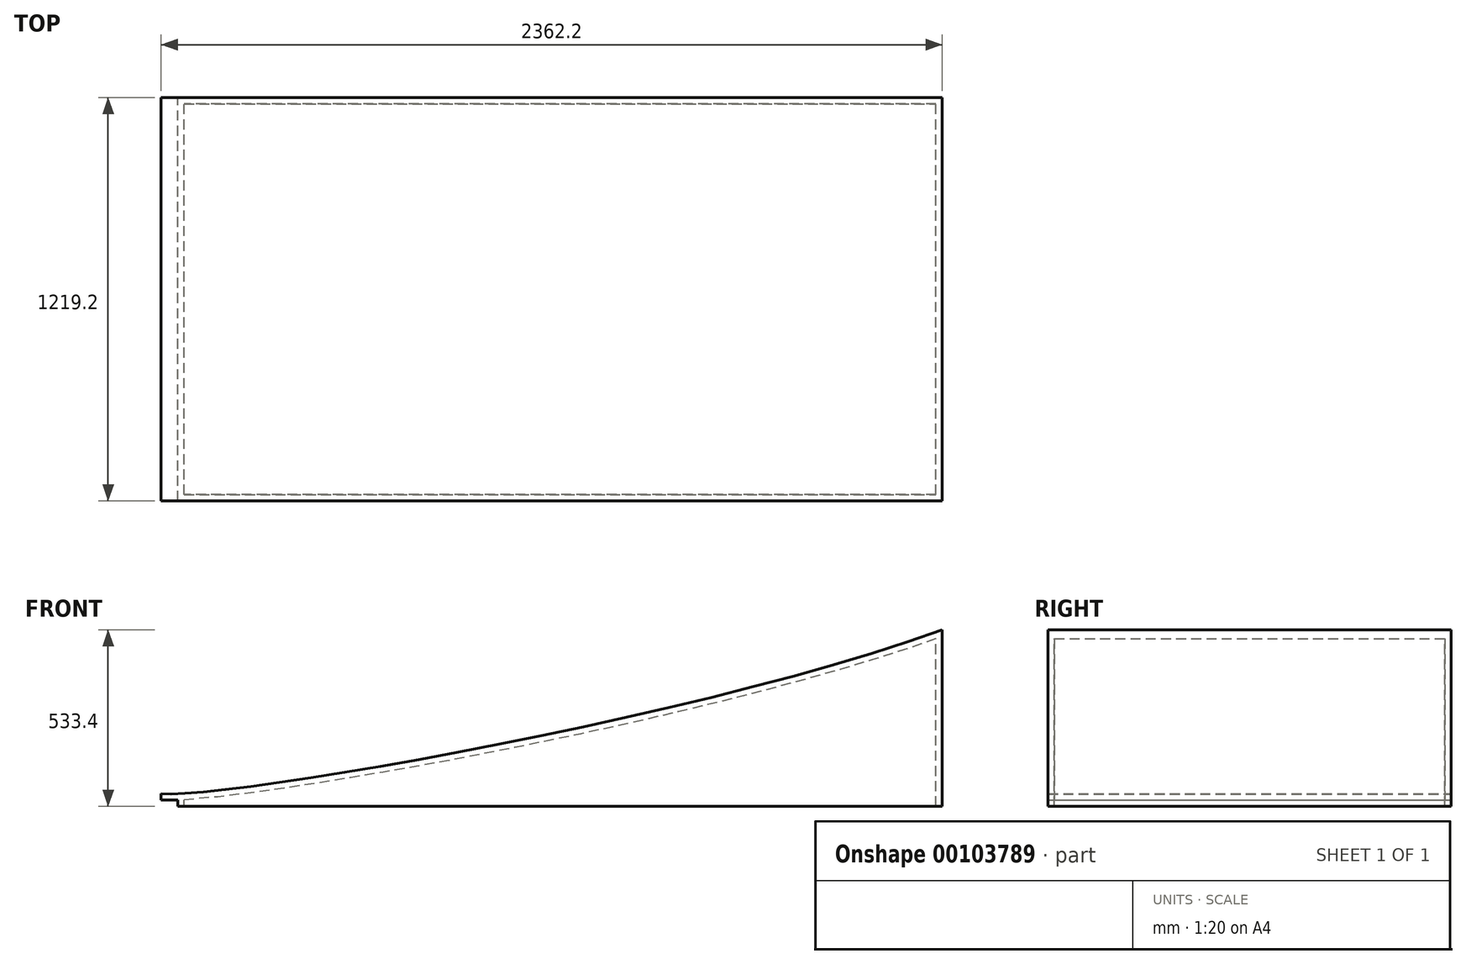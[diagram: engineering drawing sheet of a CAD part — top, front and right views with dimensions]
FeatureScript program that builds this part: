
annotation { "Feature Type Name" : "Feature", "Feature Type Description" : "" }
export const myFeature = defineFeature(function(context is Context, id is Id, definition is map)
    precondition{}
    {
        {
            var Q0;
            Q0=qCreatedBy(makeId("Front.planeOp"),FACE);
            var sketch = newSketch(context, id + "F0", { "sketchPlane" : qUnion([Q0])});
            skLineSegment(sketch, "E0", {"start": v(0, 0) * mm, "end": v(0, 533.4) * mm});
            skLineSegment(sketch, "E1", {"start": v(-2362.2, 0) * mm, "end": v(-2311.4, 0) * mm, "construction": true});
            skLineSegment(sketch, "E2", {"start": v(-2311.4, 0) * mm, "end": v(-2311.4, 19.05) * mm});
            skLineSegment(sketch, "E3", {"start": v(-2311.4, 19.05) * mm, "end": v(0, 19.05) * mm, "construction": true});
            skLineSegment(sketch, "E4", {"start": v(-2311.4, 19.05) * mm, "end": v(-2362.2, 19.05) * mm});
            skLineSegment(sketch, "E5", {"start": v(-2311.4, 0) * mm, "end": v(0, 0) * mm});
            skFitSpline(sketch, "E6", {"points": [v(0, 533.4) * mm, v(-2362.2, 38.1) * mm], "startDerivative": vector(-2287.3, -824.38) * mm, "endDerivative": vector(-518.22, 57.15) * mm});
            skLineSegment(sketch, "E7", {"start": v(-2362.2, 38.1) * mm, "end": v(-2362.2, 19.05) * mm});
            skSolve(sketch);
        }
        {
            var Q0;
            Q0=makeQuery(id+"F0.imprint","IMPRINT",FACE,{"disambiguationData":[TD([[makeQuery(id+"F0.imprint","IMPRINT",EDGE,{"derivedFrom":sQuery(id+"F0.wireOp",EDGE,"E0")}),1.0]])]});
            extrude(context, id + "F1", {"entities" : qUnion([Q0]), "depth" : 1219.2 * mm});
        }
        {
            var Q0;
            Q0=makeQuery(id+"F1.opExtrude","SWEPT_FACE",FACE,{"disambiguationData":[OSD([sQuery(id+"F0.wireOp",EDGE,"E5")])]});
            shell(context, id + "F2", {"entities" : qUnion([Q0]), "thickness" : 19.05 * mm});
        }
    });
